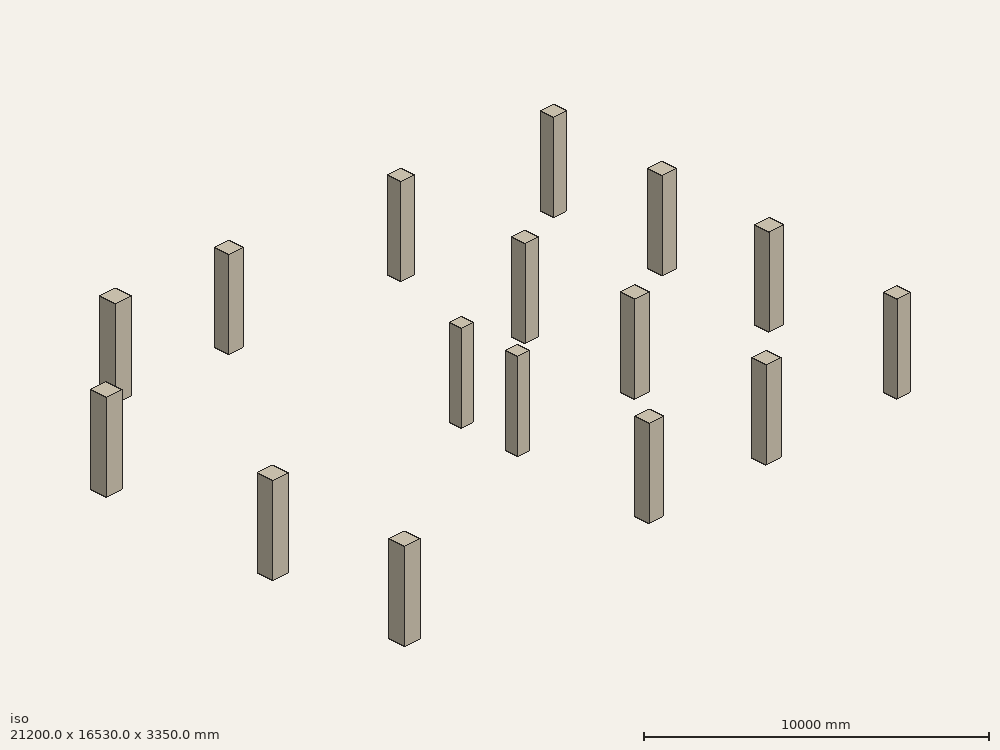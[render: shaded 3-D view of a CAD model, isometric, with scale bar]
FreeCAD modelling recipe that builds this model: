
FCSTD DOCUMENT  (FreeCAD 0.19R24291 (Git))
Label: rashidzadeh
License: All rights reserved
LicenseURL: http://en.wikipedia.org/wiki/All_rights_reserved
objects: Part::Part2DObjectPython×68, Part::FeaturePython×53, App::FeaturePython×17, App::DocumentObjectGroup×5
note: 268 computed .brp shape members not serialized (recipe doc carries the construction recipe); baked Part::Feature solids carry a one-line shape summary decoded from their .brp

FEATURE [Part::Part2DObjectPython] Line006  label="C1_Story1_CenterLine"  # Draft 2D object (typed FeaturePython)
  Area = 0
  ChamferSize = 0
  Closed = false
  End = (17740,20340,3350)
  FilletRadius = 0
  Length = 3350
  MakeFace = true
  Points = (2) [(17740,20340,0),(17740,20340,3350)]
  Start = (17740,20340,0)
  Subdivisions = 0
FEATURE [Part::Part2DObjectPython] C5512C  # Draft 2D object (typed FeaturePython)
  Height = 550
  Width = 550
FEATURE [Part::FeaturePython] Structure  label="C1_Story1"  # Arch/BIM 24 (typed FeaturePython)
  AttacherType = Attacher::AttachEngine3D
  AttachmentOffset = pos=(0,0,0) rot=(0,0,1;1.5708rad)
  Base = -> C5512C
  FaceMaker = 0
  Height = 3350
  HorizontalArea = 302500
  IfcData = attributes={"GlobalId": {"name": "GlobalId", "type": "IfcGloballyUniqueId", "is_enum": false, "enum_values": []}, "Description": {"... (+438 chars omitted),+1 more (map truncated)
  IfcType = 24
  Length = 0
  MapMode = 7
  MoveBase = false
  MoveWithHost = false
  Nodes = (2) [(17740,20340,0),(17740,20340,3350)]
  NodesOffset = 0
  Normal = (0,0,0)
  PerimeterLength = 2200
  Placement = pos=(17740,20340,0) rot=(0,0,1;1.5708rad)
  PredefinedType = 0
  Support = -> [Line006]
  VerticalArea = 7.37e+06
  Width = 200
  combos_load = Combo1 Max=2929.3594, 27006.37, 14808.13,Combo10 Max=2608.538, -98112.68, -391082.9,Combo11 Max=2657.75, -72288.26, -345375.92,+37 more (map truncated)
FEATURE [Part::Part2DObjectPython] Line007  label="C2_Story1_CenterLine"  # Draft 2D object (typed FeaturePython)
  Area = 0
  ChamferSize = 0
  Closed = false
  End = (23500,19838.5,3350)
  FilletRadius = 0
  Length = 3350
  MakeFace = true
  Points = (2) [(23500,19838.5,0),(23500,19838.5,3350)]
  Start = (23500,19838.5,0)
  Subdivisions = 0
FEATURE [Part::FeaturePython] Structure001  label="C2_Story1"  # Arch/BIM 24 (typed FeaturePython)
  AttacherType = Attacher::AttachEngine3D
  AttachmentOffset = pos=(0,0,0) rot=(0,0,1;1.5708rad)
  Base = -> C5512C
  FaceMaker = 0
  Height = 3350
  HorizontalArea = 302500
  IfcData = attributes={"GlobalId": {"name": "GlobalId", "type": "IfcGloballyUniqueId", "is_enum": false, "enum_values": []}, "Description": {"... (+438 chars omitted),+1 more (map truncated)
  IfcType = 24
  Length = 0
  MapMode = 7
  MoveBase = false
  MoveWithHost = false
  Nodes = (2) [(23500,19838.5,0),(23500,19838.5,3350)]
  NodesOffset = 0
  Normal = (0,0,0)
  PerimeterLength = 2200
  Placement = pos=(23500,19838.5,0) rot=(0,0,1;1.5708rad)
  PredefinedType = 0
  Support = -> [Line007]
  VerticalArea = 7.37e+06
  Width = 200
  combos_load = Combo1 Max=1754.8461, 12356.17, -26849.18,Combo10 Max=2143.525, -139905.36, -387343.42,Combo11 Max=2175.8338, -83310.12, -350318.73,+37 more (map truncated)
FEATURE [Part::Part2DObjectPython] Line008  label="C17_Story1_CenterLine"  # Draft 2D object (typed FeaturePython)
  Area = 0
  ChamferSize = 0
  Closed = false
  End = (23370,15250,3350)
  FilletRadius = 0
  Length = 3350
  MakeFace = true
  Points = (2) [(23370,15250,0),(23370,15250,3350)]
  Start = (23370,15250,0)
  Subdivisions = 0
FEATURE [Part::Part2DObjectPython] C6012AC  # Draft 2D object (typed FeaturePython)
  Height = 600
  Width = 600
FEATURE [Part::FeaturePython] Structure002  label="C17_Story1"  # Arch/BIM 24 (typed FeaturePython)
  AttacherType = Attacher::AttachEngine3D
  AttachmentOffset = pos=(0,0,0) rot=(0,0,1;1.5708rad)
  Base = -> C6012AC
  FaceMaker = 0
  Height = 3350
  HorizontalArea = 360000
  IfcData = attributes={"GlobalId": {"name": "GlobalId", "type": "IfcGloballyUniqueId", "is_enum": false, "enum_values": []}, "Description": {"... (+438 chars omitted),+1 more (map truncated)
  IfcType = 24
  Length = 0
  MapMode = 7
  MoveBase = false
  MoveWithHost = false
  Nodes = (2) [(23370,15250,0),(23370,15250,3350)]
  NodesOffset = 0
  Normal = (0,0,0)
  PerimeterLength = 2400
  Placement = pos=(23370,15250,0) rot=(0,0,1;1.5708rad)
  PredefinedType = 0
  Support = -> [Line008]
  VerticalArea = 8.04e+06
  Width = 200
  combos_load = Combo1 Max=1514.2218, -5536.02, -34563.49,Combo10 Max=1873.5598, -222983.25, -488160.13,Combo11 Max=1871.0673, -140666.82, -475481.05,+37 more (map truncated)
FEATURE [Part::Part2DObjectPython] Line009  label="C18_Story1_CenterLine"  # Draft 2D object (typed FeaturePython)
  Area = 0
  ChamferSize = 0
  Closed = false
  End = (23250,10750,3350)
  FilletRadius = 0
  Length = 3350
  MakeFace = true
  Points = (2) [(23250,10750,0),(23250,10750,3350)]
  Start = (23250,10750,0)
  Subdivisions = 0
FEATURE [Part::FeaturePython] Structure003  label="C18_Story1"  # Arch/BIM 24 (typed FeaturePython)
  AttacherType = Attacher::AttachEngine3D
  AttachmentOffset = pos=(0,0,0) rot=(0,0,1;1.5708rad)
  Base = -> C6012AC
  FaceMaker = 0
  Height = 3350
  HorizontalArea = 360000
  IfcData = attributes={"GlobalId": {"name": "GlobalId", "type": "IfcGloballyUniqueId", "is_enum": false, "enum_values": []}, "Description": {"... (+438 chars omitted),+1 more (map truncated)
  IfcType = 24
  Length = 0
  MapMode = 7
  MoveBase = false
  MoveWithHost = false
  Nodes = (2) [(23250,10750,0),(23250,10750,3350)]
  NodesOffset = 0
  Normal = (0,0,0)
  PerimeterLength = 2400
  Placement = pos=(23250,10750,0) rot=(0,0,1;1.5708rad)
  PredefinedType = 0
  Support = -> [Line009]
  VerticalArea = 8.04e+06
  Width = 200
  combos_load = Combo1 Max=1534.3408, 49.31, -39260.22,Combo10 Max=2051.3394, -213536.56, -457180.36,Combo11 Max=2057.4036, -133173.75, -478456.04,+37 more (map truncated)
FEATURE [Part::Part2DObjectPython] Line010  label="C5_Story1_CenterLine"  # Draft 2D object (typed FeaturePython)
  Area = 0
  ChamferSize = 0
  Closed = false
  End = (17740,5350,3350)
  FilletRadius = 0
  Length = 3350
  MakeFace = true
  Points = (2) [(17740,5350,0),(17740,5350,3350)]
  Start = (17740,5350,0)
  Subdivisions = 0
FEATURE [Part::FeaturePython] Structure004  label="C5_Story1"  # Arch/BIM 24 (typed FeaturePython)
  AttacherType = Attacher::AttachEngine3D
  AttachmentOffset = pos=(0,0,0) rot=(0,0,1;1.5708rad)
  Base = -> C6012AC
  FaceMaker = 0
  Height = 3350
  HorizontalArea = 360000
  IfcData = attributes={"GlobalId": {"name": "GlobalId", "type": "IfcGloballyUniqueId", "is_enum": false, "enum_values": []}, "Description": {"... (+438 chars omitted),+1 more (map truncated)
  IfcType = 24
  Length = 0
  MapMode = 7
  MoveBase = false
  MoveWithHost = false
  Nodes = (2) [(17740,5350,0),(17740,5350,3350)]
  NodesOffset = 0
  Normal = (0,0,0)
  PerimeterLength = 2400
  Placement = pos=(17740,5350,0) rot=(0,0,1;1.5708rad)
  PredefinedType = 0
  Support = -> [Line010]
  VerticalArea = 8.04e+06
  Width = 200
  combos_load = Combo1 Max=1623.3033, -947.79, -5177.17,Combo10 Max=1786.5067, -169313.57, -460450.33,Combo11 Max=1770.754, -135335.23, -531760.45,+37 more (map truncated)
FEATURE [Part::Part2DObjectPython] Line011  label="C6_Story1_CenterLine"  # Draft 2D object (typed FeaturePython)
  Area = 0
  ChamferSize = 0
  Closed = false
  End = (12940,5350,3350)
  FilletRadius = 0
  Length = 3350
  MakeFace = true
  Points = (2) [(12940,5350,0),(12940,5350,3350)]
  Start = (12940,5350,0)
  Subdivisions = 0
FEATURE [Part::FeaturePython] Structure005  label="C6_Story1"  # Arch/BIM 24 (typed FeaturePython)
  AttacherType = Attacher::AttachEngine3D
  AttachmentOffset = pos=(0,0,0) rot=(0,0,1;1.5708rad)
  Base = -> C6012AC
  FaceMaker = 0
  Height = 3350
  HorizontalArea = 360000
  IfcData = attributes={"GlobalId": {"name": "GlobalId", "type": "IfcGloballyUniqueId", "is_enum": false, "enum_values": []}, "Description": {"... (+438 chars omitted),+1 more (map truncated)
  IfcType = 24
  Length = 0
  MapMode = 7
  MoveBase = false
  MoveWithHost = false
  Nodes = (2) [(12940,5350,0),(12940,5350,3350)]
  NodesOffset = 0
  Normal = (0,0,0)
  PerimeterLength = 2400
  Placement = pos=(12940,5350,0) rot=(0,0,1;1.5708rad)
  PredefinedType = 0
  Support = -> [Line011]
  VerticalArea = 8.04e+06
  Width = 200
  combos_load = Combo1 Max=2458.9073, 10889.53, -106700.8,Combo10 Max=1939.8727, -132976.26, -554878.34,Combo11 Max=1860.3718, -132910.34, -622641.45,+37 more (map truncated)
FEATURE [Part::Part2DObjectPython] Line012  label="C19_Story1_CenterLine"  # Draft 2D object (typed FeaturePython)
  Area = 0
  ChamferSize = 0
  Closed = false
  End = (23100,5350,3350)
  FilletRadius = 0
  Length = 3350
  MakeFace = true
  Points = (2) [(23100,5350,0),(23100,5350,3350)]
  Start = (23100,5350,0)
  Subdivisions = 0
FEATURE [Part::Part2DObjectPython] C5512AC  # Draft 2D object (typed FeaturePython)
  Height = 550
  Width = 550
FEATURE [Part::FeaturePython] Structure006  label="C19_Story1"  # Arch/BIM 24 (typed FeaturePython)
  AttacherType = Attacher::AttachEngine3D
  AttachmentOffset = pos=(0,0,0) rot=(0,0,1;1.5708rad)
  Base = -> C5512AC
  FaceMaker = 0
  Height = 3350
  HorizontalArea = 302500
  IfcData = attributes={"GlobalId": {"name": "GlobalId", "type": "IfcGloballyUniqueId", "is_enum": false, "enum_values": []}, "Description": {"... (+438 chars omitted),+1 more (map truncated)
  IfcType = 24
  Length = 0
  MapMode = 7
  MoveBase = false
  MoveWithHost = false
  Nodes = (2) [(23100,5350,0),(23100,5350,3350)]
  NodesOffset = 0
  Normal = (0,0,0)
  PerimeterLength = 2200
  Placement = pos=(23100,5350,0) rot=(0,0,1;1.5708rad)
  PredefinedType = 0
  Support = -> [Line012]
  VerticalArea = 7.37e+06
  Width = 200
  combos_load = Combo1 Max=1051.5097, -14568.81, -35137.32,Combo10 Max=1680.8499, -155391.05, -323776.55,Combo11 Max=1698.4736, -101933.47, -370507.25,+37 more (map truncated)
FEATURE [Part::Part2DObjectPython] Line013  label="C8_Story1_CenterLine"  # Draft 2D object (typed FeaturePython)
  Area = 0
  ChamferSize = 0
  Closed = false
  End = (11240,20890,3350)
  FilletRadius = 0
  Length = 3350
  MakeFace = true
  Points = (2) [(11240,20890,0),(11240,20890,3350)]
  Start = (11240,20890,0)
  Subdivisions = 0
FEATURE [Part::Part2DObjectPython] C6012C  # Draft 2D object (typed FeaturePython)
  Height = 600
  Width = 600
FEATURE [Part::FeaturePython] Structure007  label="C8_Story1"  # Arch/BIM 24 (typed FeaturePython)
  AttacherType = Attacher::AttachEngine3D
  AttachmentOffset = pos=(0,0,0) rot=(0,0,1;1.5708rad)
  Base = -> C6012C
  FaceMaker = 0
  Height = 3350
  HorizontalArea = 360000
  IfcData = attributes={"GlobalId": {"name": "GlobalId", "type": "IfcGloballyUniqueId", "is_enum": false, "enum_values": []}, "Description": {"... (+438 chars omitted),+1 more (map truncated)
  IfcType = 24
  Length = 0
  MapMode = 7
  MoveBase = false
  MoveWithHost = false
  Nodes = (2) [(11240,20890,0),(11240,20890,3350)]
  NodesOffset = 0
  Normal = (0,0,0)
  PerimeterLength = 2400
  Placement = pos=(11240,20890,0) rot=(0,0,1;1.5708rad)
  PredefinedType = 0
  Support = -> [Line013]
  VerticalArea = 8.04e+06
  Width = 200
  combos_load = Combo1 Max=3176.7816, 67519.66, -1586.57,Combo10 Max=3690.7518, -72646.95, -573333.56,Combo11 Max=3628.5505, -82554.37, -507645.57,+37 more (map truncated)
FEATURE [Part::Part2DObjectPython] Line014  label="C9_Story1_CenterLine"  # Draft 2D object (typed FeaturePython)
  Area = 0
  ChamferSize = 0
  Closed = false
  End = (6930,21230,3350)
  FilletRadius = 0
  Length = 3350
  MakeFace = true
  Points = (2) [(6930,21230,0),(6930,21230,3350)]
  Start = (6930,21230,0)
  Subdivisions = 0
FEATURE [Part::Part2DObjectPython] C6516AC  # Draft 2D object (typed FeaturePython)
  Height = 650
  Width = 650
FEATURE [Part::FeaturePython] Structure008  label="C9_Story1"  # Arch/BIM 24 (typed FeaturePython)
  AttacherType = Attacher::AttachEngine3D
  AttachmentOffset = pos=(0,0,0) rot=(0,0,1;1.5708rad)
  Base = -> C6516AC
  FaceMaker = 0
  Height = 3350
  HorizontalArea = 422500
  IfcData = attributes={"GlobalId": {"name": "GlobalId", "type": "IfcGloballyUniqueId", "is_enum": false, "enum_values": []}, "Description": {"... (+438 chars omitted),+1 more (map truncated)
  IfcType = 24
  Length = 0
  MapMode = 7
  MoveBase = false
  MoveWithHost = false
  Nodes = (2) [(6930,21230,0),(6930,21230,3350)]
  NodesOffset = 0
  Normal = (0,0,0)
  PerimeterLength = 2600
  Placement = pos=(6930,21230,0) rot=(0,0,1;1.5708rad)
  PredefinedType = 0
  Support = -> [Line014]
  VerticalArea = 8.71e+06
  Width = 200
  combos_load = Combo1 Max=3178.5002, 13656.36, 31223.41,Combo10 Max=2579.0077, -108238.08, -657320.49,Combo11 Max=2529.7417, -170319.15, -568803.46,+37 more (map truncated)
FEATURE [Part::Part2DObjectPython] Line015  label="C10_Story1_CenterLine"  # Draft 2D object (typed FeaturePython)
  Area = 0
  ChamferSize = 0
  Closed = false
  End = (2900,17580,3350)
  FilletRadius = 0
  Length = 3350
  MakeFace = true
  Points = (2) [(2900,17580,0),(2900,17580,3350)]
  Start = (2900,17580,0)
  Subdivisions = 0
FEATURE [Part::FeaturePython] Structure009  label="C10_Story1"  # Arch/BIM 24 (typed FeaturePython)
  AttacherType = Attacher::AttachEngine3D
  AttachmentOffset = pos=(0,0,0) rot=(0,0,1;1.5708rad)
  Base = -> C6516AC
  FaceMaker = 0
  Height = 3350
  HorizontalArea = 422500
  IfcData = attributes={"GlobalId": {"name": "GlobalId", "type": "IfcGloballyUniqueId", "is_enum": false, "enum_values": []}, "Description": {"... (+438 chars omitted),+1 more (map truncated)
  IfcType = 24
  Length = 0
  MapMode = 7
  MoveBase = false
  MoveWithHost = false
  Nodes = (2) [(2900,17580,0),(2900,17580,3350)]
  NodesOffset = 0
  Normal = (0,0,0)
  PerimeterLength = 2600
  Placement = pos=(2900,17580,0) rot=(0,0,1;1.5708rad)
  PredefinedType = 0
  Support = -> [Line015]
  VerticalArea = 8.71e+06
  Width = 200
  combos_load = Combo1 Max=4513.1788, 66434.1, 128004.31,Combo10 Max=3493.9652, -29609.04, -415032.95,Combo11 Max=3559.9915, -136385.01, -369140.23,+37 more (map truncated)
FEATURE [Part::Part2DObjectPython] Line016  label="C16_Story1_CenterLine"  # Draft 2D object (typed FeaturePython)
  Area = 0
  ChamferSize = 0
  Closed = false
  End = (2900,5350,3350)
  FilletRadius = 0
  Length = 3350
  MakeFace = true
  Points = (2) [(2900,5350,0),(2900,5350,3350)]
  Start = (2900,5350,0)
  Subdivisions = 0
FEATURE [Part::Part2DObjectPython] C6516A  # Draft 2D object (typed FeaturePython)
  Height = 650
  Width = 650
FEATURE [Part::FeaturePython] Structure010  label="C16_Story1"  # Arch/BIM 24 (typed FeaturePython)
  AttacherType = Attacher::AttachEngine3D
  AttachmentOffset = pos=(0,0,0) rot=(0,0,1;1.5708rad)
  Base = -> C6516A
  FaceMaker = 0
  Height = 3350
  HorizontalArea = 422500
  IfcData = attributes={"GlobalId": {"name": "GlobalId", "type": "IfcGloballyUniqueId", "is_enum": false, "enum_values": []}, "Description": {"... (+438 chars omitted),+1 more (map truncated)
  IfcType = 24
  Length = 0
  MapMode = 7
  MoveBase = false
  MoveWithHost = false
  Nodes = (2) [(2900,5350,0),(2900,5350,3350)]
  NodesOffset = 0
  Normal = (0,0,0)
  PerimeterLength = 2600
  Placement = pos=(2900,5350,0) rot=(0,0,1;1.5708rad)
  PredefinedType = 0
  Support = -> [Line016]
  VerticalArea = 8.71e+06
  Width = 200
  combos_load = Combo1 Max=2178.0668, -11443.95, 110544.97,Combo10 Max=2207.6537, -146873.33, -349025.65,Combo11 Max=2312.863, -249404.95, -427796.67,+37 more (map truncated)
FEATURE [Part::Part2DObjectPython] Line017  label="C12_Story1_CenterLine"  # Draft 2D object (typed FeaturePython)
  Area = 0
  ChamferSize = 0
  Closed = false
  End = (17740,10750,3350)
  FilletRadius = 0
  Length = 3350
  MakeFace = true
  Points = (2) [(17740,10750,0),(17740,10750,3350)]
  Start = (17740,10750,0)
  Subdivisions = 0
FEATURE [Part::FeaturePython] Structure011  label="C12_Story1"  # Arch/BIM 24 (typed FeaturePython)
  AttacherType = Attacher::AttachEngine3D
  AttachmentOffset = pos=(0,0,0) rot=(0,0,1;1.5708rad)
  Base = -> C6012C
  FaceMaker = 0
  Height = 3350
  HorizontalArea = 360000
  IfcData = attributes={"GlobalId": {"name": "GlobalId", "type": "IfcGloballyUniqueId", "is_enum": false, "enum_values": []}, "Description": {"... (+438 chars omitted),+1 more (map truncated)
  IfcType = 24
  Length = 0
  MapMode = 7
  MoveBase = false
  MoveWithHost = false
  Nodes = (2) [(17740,10750,0),(17740,10750,3350)]
  NodesOffset = 0
  Normal = (0,0,0)
  PerimeterLength = 2400
  Placement = pos=(17740,10750,0) rot=(0,0,1;1.5708rad)
  PredefinedType = 0
  Support = -> [Line017]
  VerticalArea = 8.04e+06
  Width = 200
  combos_load = Combo1 Max=2372.5516, -20700, 4401.45,Combo10 Max=2415.4815, -204900.61, -476224.38,Combo11 Max=2407.8904, -168225.73, -499976.16,+37 more (map truncated)
FEATURE [Part::Part2DObjectPython] Line018  label="C13_Story1_CenterLine"  # Draft 2D object (typed FeaturePython)
  Area = 0
  ChamferSize = 0
  Closed = false
  End = (17740,15250,3350)
  FilletRadius = 0
  Length = 3350
  MakeFace = true
  Points = (2) [(17740,15250,0),(17740,15250,3350)]
  Start = (17740,15250,0)
  Subdivisions = 0
FEATURE [Part::FeaturePython] Structure012  label="C13_Story1"  # Arch/BIM 24 (typed FeaturePython)
  AttacherType = Attacher::AttachEngine3D
  AttachmentOffset = pos=(0,0,0) rot=(0,0,1;1.5708rad)
  Base = -> C5512C
  FaceMaker = 0
  Height = 3350
  HorizontalArea = 302500
  IfcData = attributes={"GlobalId": {"name": "GlobalId", "type": "IfcGloballyUniqueId", "is_enum": false, "enum_values": []}, "Description": {"... (+438 chars omitted),+1 more (map truncated)
  IfcType = 24
  Length = 0
  MapMode = 7
  MoveBase = false
  MoveWithHost = false
  Nodes = (2) [(17740,15250,0),(17740,15250,3350)]
  NodesOffset = 0
  Normal = (0,0,0)
  PerimeterLength = 2200
  Placement = pos=(17740,15250,0) rot=(0,0,1;1.5708rad)
  PredefinedType = 0
  Support = -> [Line018]
  VerticalArea = 7.37e+06
  Width = 200
  combos_load = Combo1 Max=2562.7432, -8357.02, -515.48,Combo10 Max=2113.2435, -155815.97, -358125.31,Combo11 Max=2129.9271, -128933.56, -347442.14,+37 more (map truncated)
FEATURE [Part::Part2DObjectPython] Line019  label="C14_Story1_CenterLine"  # Draft 2D object (typed FeaturePython)
  Area = 0
  ChamferSize = 0
  Closed = false
  End = (12940,10750,3350)
  FilletRadius = 0
  Length = 3350
  MakeFace = true
  Points = (2) [(12940,10750,0),(12940,10750,3350)]
  Start = (12940,10750,0)
  Subdivisions = 0
FEATURE [Part::Part2DObjectPython] C5012AC  # Draft 2D object (typed FeaturePython)
  Height = 500
  Width = 500
FEATURE [Part::FeaturePython] Structure013  label="C14_Story1"  # Arch/BIM 24 (typed FeaturePython)
  AttacherType = Attacher::AttachEngine3D
  AttachmentOffset = pos=(0,0,0) rot=(0,0,1;3.14159rad)
  Base = -> C5012AC
  FaceMaker = 0
  Height = 3350
  HorizontalArea = 250000
  IfcData = attributes={"GlobalId": {"name": "GlobalId", "type": "IfcGloballyUniqueId", "is_enum": false, "enum_values": []}, "Description": {"... (+438 chars omitted),+1 more (map truncated)
  IfcType = 24
  Length = 0
  MapMode = 7
  MoveBase = false
  MoveWithHost = false
  Nodes = (2) [(12940,10750,0),(12940,10750,3350)]
  NodesOffset = 0
  Normal = (0,0,0)
  PerimeterLength = 2000
  Placement = pos=(12940,10750,0) rot=(0,0,1;3.14159rad)
  PredefinedType = 0
  Support = -> [Line019]
  VerticalArea = 6.7e+06
  Width = 200
  combos_load = Combo1 Max=2582.1087, 172.69, -72462.15,Combo10 Max=2432.6339, -96294.19, -372624.2,Combo11 Max=2403.0715, -96603.51, -385451.48,+37 more (map truncated)
FEATURE [Part::Part2DObjectPython] Line020  label="C15_Story1_CenterLine"  # Draft 2D object (typed FeaturePython)
  Area = 0
  ChamferSize = 0
  Closed = false
  End = (12940,13050,3350)
  FilletRadius = 0
  Length = 3350
  MakeFace = true
  Points = (2) [(12940,13050,0),(12940,13050,3350)]
  Start = (12940,13050,0)
  Subdivisions = 0
FEATURE [Part::Part2DObjectPython] C5016A  # Draft 2D object (typed FeaturePython)
  Height = 500
  Width = 500
FEATURE [Part::FeaturePython] Structure014  label="C15_Story1"  # Arch/BIM 24 (typed FeaturePython)
  AttacherType = Attacher::AttachEngine3D
  AttachmentOffset = pos=(0,0,0) rot=(0,0,1;3.14159rad)
  Base = -> C5016A
  FaceMaker = 0
  Height = 3350
  HorizontalArea = 250000
  IfcData = attributes={"GlobalId": {"name": "GlobalId", "type": "IfcGloballyUniqueId", "is_enum": false, "enum_values": []}, "Description": {"... (+438 chars omitted),+1 more (map truncated)
  IfcType = 24
  Length = 0
  MapMode = 7
  MoveBase = false
  MoveWithHost = false
  Nodes = (2) [(12940,13050,0),(12940,13050,3350)]
  NodesOffset = 0
  Normal = (0,0,0)
  PerimeterLength = 2000
  Placement = pos=(12940,13050,0) rot=(0,0,1;3.14159rad)
  PredefinedType = 0
  Support = -> [Line020]
  VerticalArea = 6.7e+06
  Width = 200
  combos_load = Combo1 Max=3210.485, -73329.89, -94104.41,Combo10 Max=2840.0423, -210175.6, -361309.23,Combo11 Max=2844.4131, -210015.24, -363099.71,+37 more (map truncated)
FEATURE [Part::Part2DObjectPython] Line021  # Draft 2D object (typed FeaturePython)
  Area = 0
  ChamferSize = 0
  Closed = false
  End = (11240,20890,0)
  FilletRadius = 0
  Length = 4323.39
  MakeFace = true
  Points = (2) [(6930,21230,0),(11240,20890,0)]
  Start = (6930,21230,0)
  Subdivisions = 0
  type = Beam
FEATURE [Part::Part2DObjectPython] Line022  # Draft 2D object (typed FeaturePython)
  Area = 0
  ChamferSize = 0
  Closed = false
  End = (17740,20340,0)
  FilletRadius = 0
  Length = 6523.23
  MakeFace = true
  Points = (2) [(11240,20890,0),(17740,20340,0)]
  Start = (11240,20890,0)
  Subdivisions = 0
  type = Beam
FEATURE [Part::Part2DObjectPython] Line023  # Draft 2D object (typed FeaturePython)
  Area = 0
  ChamferSize = 0
  Closed = false
  End = (23500,19838.5,0)
  FilletRadius = 0
  Length = 5781.79
  MakeFace = true
  Points = (2) [(17740,20340,0),(23500,19838.5,0)]
  Start = (17740,20340,0)
  Subdivisions = 0
  type = Beam
FEATURE [Part::Part2DObjectPython] Line024  # Draft 2D object (typed FeaturePython)
  Area = 0
  ChamferSize = 0
  Closed = false
  End = (23500,19838.5,0)
  FilletRadius = 0
  Length = 4590.3
  MakeFace = true
  Points = (2) [(23370,15250,0),(23500,19838.5,0)]
  Start = (23370,15250,0)
  Subdivisions = 0
  type = Beam
FEATURE [Part::Part2DObjectPython] Line025  # Draft 2D object (typed FeaturePython)
  Area = 0
  ChamferSize = 0
  Closed = false
  End = (23370,15250,0)
  FilletRadius = 0
  Length = 4501.6
  MakeFace = true
  Points = (2) [(23250,10750,0),(23370,15250,0)]
  Start = (23250,10750,0)
  Subdivisions = 0
  type = Beam
FEATURE [Part::Part2DObjectPython] Line026  # Draft 2D object (typed FeaturePython)
  Area = 0
  ChamferSize = 0
  Closed = false
  End = (23100,5350,0)
  FilletRadius = 0
  Length = 5360
  MakeFace = true
  Points = (2) [(17740,5350,0),(23100,5350,0)]
  Start = (17740,5350,0)
  Subdivisions = 0
  type = Beam
FEATURE [Part::Part2DObjectPython] Line027  # Draft 2D object (typed FeaturePython)
  Area = 0
  ChamferSize = 0
  Closed = false
  End = (17740,5350,0)
  FilletRadius = 0
  Length = 4800
  MakeFace = true
  Points = (2) [(12940,5350,0),(17740,5350,0)]
  Start = (12940,5350,0)
  Subdivisions = 0
  type = Beam
FEATURE [Part::Part2DObjectPython] Line028  # Draft 2D object (typed FeaturePython)
  Area = 0
  ChamferSize = 0
  Closed = false
  End = (12940,5350,0)
  FilletRadius = 0
  Length = 10040
  MakeFace = true
  Points = (2) [(2900,5350,0),(12940,5350,0)]
  Start = (2900,5350,0)
  Subdivisions = 0
  type = Beam
FEATURE [Part::Part2DObjectPython] Line029  # Draft 2D object (typed FeaturePython)
  Area = 0
  ChamferSize = 0
  Closed = false
  End = (2900,10750,0)
  FilletRadius = 0
  Length = 5400
  MakeFace = true
  Points = (2) [(2900,5350,0),(2900,10750,0)]
  Start = (2900,5350,0)
  Subdivisions = 0
  type = Beam
FEATURE [Part::Part2DObjectPython] Line030  # Draft 2D object (typed FeaturePython)
  Area = 0
  ChamferSize = 0
  Closed = false
  End = (2900,17580,0)
  FilletRadius = 0
  Length = 6830
  MakeFace = true
  Points = (2) [(2900,10750,0),(2900,17580,0)]
  Start = (2900,10750,0)
  Subdivisions = 0
  type = Beam
FEATURE [Part::Part2DObjectPython] Line031  # Draft 2D object (typed FeaturePython)
  Area = 0
  ChamferSize = 0
  Closed = false
  End = (6930,21230,0)
  FilletRadius = 0
  Length = 5437.22
  MakeFace = true
  Points = (2) [(2900,17580,0),(6930,21230,0)]
  Start = (2900,17580,0)
  Subdivisions = 0
  type = Beam
FEATURE [Part::Part2DObjectPython] Line032  # Draft 2D object (typed FeaturePython)
  Area = 0
  ChamferSize = 0
  Closed = false
  End = (17740,10750,0)
  FilletRadius = 0
  Length = 5400
  MakeFace = true
  Points = (2) [(17740,5350,0),(17740,10750,0)]
  Start = (17740,5350,0)
  Subdivisions = 0
  type = Beam
FEATURE [Part::Part2DObjectPython] Line033  # Draft 2D object (typed FeaturePython)
  Area = 0
  ChamferSize = 0
  Closed = false
  End = (17740,15250,0)
  FilletRadius = 0
  Length = 4500
  MakeFace = true
  Points = (2) [(17740,10750,0),(17740,15250,0)]
  Start = (17740,10750,0)
  Subdivisions = 0
  type = Beam
FEATURE [Part::Part2DObjectPython] Line034  # Draft 2D object (typed FeaturePython)
  Area = 0
  ChamferSize = 0
  Closed = false
  End = (12940,10750,0)
  FilletRadius = 0
  Length = 5400
  MakeFace = true
  Points = (2) [(12940,5350,0),(12940,10750,0)]
  Start = (12940,5350,0)
  Subdivisions = 0
  type = Beam
FEATURE [Part::Part2DObjectPython] Line035  # Draft 2D object (typed FeaturePython)
  Area = 0
  ChamferSize = 0
  Closed = false
  End = (12940,13050,0)
  FilletRadius = 0
  Length = 2300
  MakeFace = true
  Points = (2) [(12940,10750,0),(12940,13050,0)]
  Start = (12940,10750,0)
  Subdivisions = 0
  type = Beam
FEATURE [Part::Part2DObjectPython] Line036  # Draft 2D object (typed FeaturePython)
  Area = 0
  ChamferSize = 0
  Closed = false
  End = (12940,13050,0)
  FilletRadius = 0
  Length = 8022.19
  MakeFace = true
  Points = (2) [(11240,20890,0),(12940,13050,0)]
  Start = (11240,20890,0)
  Subdivisions = 0
  type = Beam
FEATURE [Part::Part2DObjectPython] Line037  # Draft 2D object (typed FeaturePython)
  Area = 0
  ChamferSize = 0
  Closed = false
  End = (23250,10750,0)
  FilletRadius = 0
  Length = 5510
  MakeFace = true
  Points = (2) [(17740,10750,0),(23250,10750,0)]
  Start = (17740,10750,0)
  Subdivisions = 0
  type = Beam
FEATURE [Part::Part2DObjectPython] Line038  # Draft 2D object (typed FeaturePython)
  Area = 0
  ChamferSize = 0
  Closed = false
  End = (17740,10750,0)
  FilletRadius = 0
  Length = 4800
  MakeFace = true
  Points = (2) [(12940,10750,0),(17740,10750,0)]
  Start = (12940,10750,0)
  Subdivisions = 0
  type = Beam
FEATURE [Part::Part2DObjectPython] Line039  # Draft 2D object (typed FeaturePython)
  Area = 0
  ChamferSize = 0
  Closed = false
  End = (12940,10750,0)
  FilletRadius = 0
  Length = 10040
  MakeFace = true
  Points = (2) [(2900,10750,0),(12940,10750,0)]
  Start = (2900,10750,0)
  Subdivisions = 0
  type = Beam
FEATURE [Part::Part2DObjectPython] Line040  # Draft 2D object (typed FeaturePython)
  Area = 0
  ChamferSize = 0
  Closed = false
  End = (12940,13050,0)
  FilletRadius = 0
  Length = 11014.6
  MakeFace = true
  Points = (2) [(2900,17580,0),(12940,13050,0)]
  Start = (2900,17580,0)
  Subdivisions = 0
  type = Beam
FEATURE [Part::Part2DObjectPython] Line041  # Draft 2D object (typed FeaturePython)
  Area = 0
  ChamferSize = 0
  Closed = false
  End = (23370,15250,0)
  FilletRadius = 0
  Length = 5630
  MakeFace = true
  Points = (2) [(17740,15250,0),(23370,15250,0)]
  Start = (17740,15250,0)
  Subdivisions = 0
  type = Beam
FEATURE [Part::Part2DObjectPython] Line042  label="C11_Story1_CenterLine"  # Draft 2D object (typed FeaturePython)
  Area = 0
  ChamferSize = 0
  Closed = false
  End = (2900,10750,3350)
  FilletRadius = 0
  Length = 3350
  MakeFace = true
  Points = (2) [(2900,10750,0),(2900,10750,3350)]
  Start = (2900,10750,0)
  Subdivisions = 0
FEATURE [Part::FeaturePython] Structure015  label="C11_Story1"  # Arch/BIM 24 (typed FeaturePython)
  AttacherType = Attacher::AttachEngine3D
  AttachmentOffset = pos=(0,0,0) rot=(0,0,1;1.5708rad)
  Base = -> C6516A
  FaceMaker = 0
  Height = 3350
  HorizontalArea = 422500
  IfcData = attributes={"GlobalId": {"name": "GlobalId", "type": "IfcGloballyUniqueId", "is_enum": false, "enum_values": []}, "Description": {"... (+438 chars omitted),+1 more (map truncated)
  IfcType = 24
  Length = 0
  MapMode = 7
  MoveBase = false
  MoveWithHost = false
  Nodes = (2) [(2900,10750,0),(2900,10750,3350)]
  NodesOffset = 0
  Normal = (0,0,0)
  PerimeterLength = 2600
  Placement = pos=(2900,10750,0) rot=(0,0,1;1.5708rad)
  PredefinedType = 0
  Support = -> [Line042]
  VerticalArea = 8.71e+06
  Width = 200
  combos_load = Combo1 Max=3352.5419, -47728.92, 119986.56,Combo10 Max=3085.1187, -203250.05, -354468.47,Combo11 Max=3033.9869, -319766.11, -381702.35,+37 more (map truncated)
FEATURE [App::DocumentObjectGroup] Columns
  Group = -> [Structure,Structure001,Structure002,Structure003,Structure004,Structure005,Structure006,Structure007,Structure008,Structure009,Structure010,Structure011,Structure012,Structure013,Structure014,Structure015]
FEATURE [Part::Part2DObjectPython] Line043  # Draft 2D object (typed FeaturePython)
  Area = 0
  ChamferSize = 0
  Closed = false
  End = (17740,13050,0)
  FilletRadius = 0
  Length = 4800
  MakeFace = true
  Points = (2) [(12940,13050,0),(17740,13050,0)]
  Start = (12940,13050,0)
  Subdivisions = 0
  type = Beam
FEATURE [Part::Part2DObjectPython] Line047  # Draft 2D object (typed FeaturePython)
  Area = 0
  ChamferSize = 0
  Closed = false
  End = (17740,20340,0)
  FilletRadius = 0
  Length = 5090
  MakeFace = true
  Points = (2) [(17740,15250,0),(17740,20340,0)]
  Start = (17740,15250,0)
  Subdivisions = 0
  type = Beam
FEATURE [Part::Part2DObjectPython] Line048  # Draft 2D object (typed FeaturePython)
  Area = 0
  ChamferSize = 0
  Closed = false
  End = (23250,10750,0)
  FilletRadius = 0
  Length = 5402.08
  MakeFace = true
  Points = (2) [(23100,5350,0),(23250,10750,0)]
  Start = (23100,5350,0)
  Subdivisions = 0
  type = Beam
FEATURE [App::DocumentObjectGroup] Beams
  Group = -> [Line021,Line022,Line023,Line024,Line025,Line026,Line027,Line028,Line029,Line030,Line031,Line032,Line033,Line034,Line035,Line036,Line037,Line038,Line039,Line040,Line041,Line043,Line047,Line048]
FEATURE [App::FeaturePython] Safe  # WARN: FeaturePython — macro-defined, semantics opaque (R4)
  input = <path>
  output = <path>
FEATURE [Part::Part2DObjectPython] Wire  # Draft 2D object (typed FeaturePython)
  Area = 0
  ChamferSize = 0
  Closed = false
  End = (2900,17580,0)
  FilletRadius = 0
  Length = 12230
  MakeFace = false
  Points = (3) [(2900,5350,0),(2900,10750,0),(2900,17580,0)]
  Start = (2900,5350,0)
  Subdivisions = 0
FEATURE [Part::FeaturePython] BaseFoundation  # Arch/BIM 77 (typed FeaturePython)
  Base = -> Wire
  HorizontalArea = 0
  IfcData = attributes={"GlobalId": {"name": "GlobalId", "type": "IfcGloballyUniqueId", "is_enum": false, "enum_values": []}, "Description": {"... (+511 chars omitted),+1 more (map truncated)
  IfcType = 77
  MoveBase = false
  MoveWithHost = false
  PerimeterLength = 0
  PredefinedType = 0
  VerticalArea = 0
  align = 0
  design_type = 0
  fc = 25000
  final_wire_first_point = (0,0,0)
  final_wire_last_point = (0,0,0)
  height = 1000
  ks = 2
  layer = 1
  left_width = 500
  right_width = 500
  width = 1000
FEATURE [Part::Part2DObjectPython] Wire001  # Draft 2D object (typed FeaturePython)
  Area = 0
  ChamferSize = 0
  Closed = false
  End = (23100,5350,0)
  FilletRadius = 0
  Length = 20200
  MakeFace = false
  Points = (4) [(2900,5350,0),(12940,5350,0),(17740,5350,0),(23100,5350,0)]
  Start = (2900,5350,0)
  Subdivisions = 0
FEATURE [Part::FeaturePython] BaseFoundation001  # Arch/BIM 77 (typed FeaturePython)
  Base = -> Wire001
  HorizontalArea = 0
  IfcData = attributes={"GlobalId": {"name": "GlobalId", "type": "IfcGloballyUniqueId", "is_enum": false, "enum_values": []}, "Description": {"... (+511 chars omitted),+1 more (map truncated)
  IfcType = 77
  MoveBase = false
  MoveWithHost = false
  PerimeterLength = 0
  PredefinedType = 0
  VerticalArea = 0
  align = 0
  design_type = 0
  fc = 25000
  final_wire_first_point = (0,0,0)
  final_wire_last_point = (0,0,0)
  height = 1000
  ks = 2
  layer = 0
  left_width = 500
  right_width = 500
  width = 1000
FEATURE [Part::Part2DObjectPython] Wire002  # Draft 2D object (typed FeaturePython)
  Area = 0
  ChamferSize = 0
  Closed = false
  End = (23250,10750,0)
  FilletRadius = 0
  Length = 20350
  MakeFace = false
  Points = (4) [(2900,10750,0),(12940,10750,0),(17740,10750,0),(23250,10750,0)]
  Start = (2900,10750,0)
  Subdivisions = 0
FEATURE [Part::FeaturePython] BaseFoundation002  # Arch/BIM 77 (typed FeaturePython)
  Base = -> Wire002
  HorizontalArea = 0
  IfcData = attributes={"GlobalId": {"name": "GlobalId", "type": "IfcGloballyUniqueId", "is_enum": false, "enum_values": []}, "Description": {"... (+511 chars omitted),+1 more (map truncated)
  IfcType = 77
  MoveBase = false
  MoveWithHost = false
  PerimeterLength = 0
  PredefinedType = 0
  VerticalArea = 0
  align = 0
  design_type = 0
  fc = 25000
  final_wire_first_point = (0,0,0)
  final_wire_last_point = (0,0,0)
  height = 1000
  ks = 2
  layer = 0
  left_width = 500
  right_width = 500
  width = 1000
FEATURE [Part::Part2DObjectPython] Line  # Draft 2D object (typed FeaturePython)
  Area = 0
  ChamferSize = 0
  Closed = false
  End = (6930,21230,0)
  FilletRadius = 0
  Length = 5437.22
  MakeFace = false
  Points = (2) [(2900,17580,0),(6930,21230,0)]
  Start = (2900,17580,0)
  Subdivisions = 0
FEATURE [Part::FeaturePython] BaseFoundation003  # Arch/BIM 77 (typed FeaturePython)
  Base = -> Line
  HorizontalArea = 0
  IfcData = attributes={"GlobalId": {"name": "GlobalId", "type": "IfcGloballyUniqueId", "is_enum": false, "enum_values": []}, "Description": {"... (+511 chars omitted),+1 more (map truncated)
  IfcType = 77
  MoveBase = false
  MoveWithHost = false
  PerimeterLength = 0
  PredefinedType = 0
  VerticalArea = 0
  align = 0
  design_type = 0
  fc = 25000
  final_wire_first_point = (0,0,0)
  final_wire_last_point = (0,0,0)
  height = 1000
  ks = 2
  layer = 0
  left_width = 500
  right_width = 500
  width = 1000
FEATURE [Part::Part2DObjectPython] Wire003  # Draft 2D object (typed FeaturePython)
  Area = 0
  ChamferSize = 0
  Closed = false
  End = (17740,13050,0)
  FilletRadius = 0
  Length = 15814.6
  MakeFace = false
  Points = (3) [(2900,17580,0),(12940,13050,0),(17740,13050,0)]
  Start = (2900,17580,0)
  Subdivisions = 0
FEATURE [Part::FeaturePython] BaseFoundation004  # Arch/BIM 77 (typed FeaturePython)
  Base = -> Wire003
  HorizontalArea = 0
  IfcData = attributes={"GlobalId": {"name": "GlobalId", "type": "IfcGloballyUniqueId", "is_enum": false, "enum_values": []}, "Description": {"... (+511 chars omitted),+1 more (map truncated)
  IfcType = 77
  MoveBase = false
  MoveWithHost = false
  PerimeterLength = 0
  PredefinedType = 0
  VerticalArea = 0
  align = 0
  design_type = 0
  fc = 25000
  final_wire_first_point = (0,0,0)
  final_wire_last_point = (0,0,0)
  height = 1000
  ks = 2
  layer = 0
  left_width = 500
  right_width = 500
  width = 1000
FEATURE [Part::Part2DObjectPython] Wire004  # Draft 2D object (typed FeaturePython)
  Area = 0
  ChamferSize = 0
  Closed = false
  End = (23500,19838.5,0)
  FilletRadius = 0
  Length = 16628.4
  MakeFace = false
  Points = (4) [(6930,21230,0),(11240,20890,0),(17740,20340,0),(23500,19838.5,0)]
  Start = (6930,21230,0)
  Subdivisions = 0
FEATURE [Part::FeaturePython] BaseFoundation005  # Arch/BIM 77 (typed FeaturePython)
  Base = -> Wire004
  HorizontalArea = 0
  IfcData = attributes={"GlobalId": {"name": "GlobalId", "type": "IfcGloballyUniqueId", "is_enum": false, "enum_values": []}, "Description": {"... (+511 chars omitted),+1 more (map truncated)
  IfcType = 77
  MoveBase = false
  MoveWithHost = false
  PerimeterLength = 0
  PredefinedType = 0
  VerticalArea = 0
  align = 0
  design_type = 0
  fc = 25000
  final_wire_first_point = (0,0,0)
  final_wire_last_point = (0,0,0)
  height = 1000
  ks = 2
  layer = 0
  left_width = 500
  right_width = 500
  width = 1000
FEATURE [Part::Part2DObjectPython] Wire005  # Draft 2D object (typed FeaturePython)
  Area = 0
  ChamferSize = 0
  Closed = false
  End = (12940,5350,0)
  FilletRadius = 0
  Length = 15722.2
  MakeFace = false
  Points = (4) [(11240,20890,0),(12940,13050,0),(12940,10750,0),(12940,5350,0)]
  Start = (11240,20890,0)
  Subdivisions = 0
FEATURE [Part::FeaturePython] BaseFoundation006  # Arch/BIM 77 (typed FeaturePython)
  Base = -> Wire005
  HorizontalArea = 0
  IfcData = attributes={"GlobalId": {"name": "GlobalId", "type": "IfcGloballyUniqueId", "is_enum": false, "enum_values": []}, "Description": {"... (+511 chars omitted),+1 more (map truncated)
  IfcType = 77
  MoveBase = false
  MoveWithHost = false
  PerimeterLength = 0
  PredefinedType = 0
  VerticalArea = 0
  align = 0
  design_type = 0
  fc = 25000
  final_wire_first_point = (0,0,0)
  final_wire_last_point = (0,0,0)
  height = 1000
  ks = 2
  layer = 1
  left_width = 500
  right_width = 500
  width = 1000
FEATURE [Part::Part2DObjectPython] Wire006  # Draft 2D object (typed FeaturePython)
  Area = 0
  ChamferSize = 0
  Closed = false
  End = (17740,20340,0)
  FilletRadius = 0
  Length = 14990
  MakeFace = false
  Points = (4) [(17740,5350,0),(17740,10750,0),(17740,15250,0),(17740,20340,0)]
  Start = (17740,5350,0)
  Subdivisions = 0
FEATURE [Part::FeaturePython] BaseFoundation007  # Arch/BIM 77 (typed FeaturePython)
  Base = -> Wire006
  HorizontalArea = 0
  IfcData = attributes={"GlobalId": {"name": "GlobalId", "type": "IfcGloballyUniqueId", "is_enum": false, "enum_values": []}, "Description": {"... (+511 chars omitted),+1 more (map truncated)
  IfcType = 77
  MoveBase = false
  MoveWithHost = false
  PerimeterLength = 0
  PredefinedType = 0
  VerticalArea = 0
  align = 0
  design_type = 0
  fc = 25000
  final_wire_first_point = (0,0,0)
  final_wire_last_point = (0,0,0)
  height = 1000
  ks = 2
  layer = 1
  left_width = 500
  right_width = 500
  width = 1000
FEATURE [Part::Part2DObjectPython] Line049  # Draft 2D object (typed FeaturePython)
  Area = 0
  ChamferSize = 0
  Closed = false
  End = (23370,15250,0)
  FilletRadius = 0
  Length = 5630
  MakeFace = false
  Points = (2) [(17740,15250,0),(23370,15250,0)]
  Start = (17740,15250,0)
  Subdivisions = 0
FEATURE [Part::FeaturePython] BaseFoundation008  # Arch/BIM 77 (typed FeaturePython)
  Base = -> Line049
  HorizontalArea = 0
  IfcData = attributes={"GlobalId": {"name": "GlobalId", "type": "IfcGloballyUniqueId", "is_enum": false, "enum_values": []}, "Description": {"... (+511 chars omitted),+1 more (map truncated)
  IfcType = 77
  MoveBase = false
  MoveWithHost = false
  PerimeterLength = 0
  PredefinedType = 0
  VerticalArea = 0
  align = 0
  design_type = 0
  fc = 25000
  final_wire_first_point = (0,0,0)
  final_wire_last_point = (0,0,0)
  height = 1000
  ks = 2
  layer = 0
  left_width = 500
  right_width = 500
  width = 1000
FEATURE [Part::Part2DObjectPython] Wire007  # Draft 2D object (typed FeaturePython)
  Area = 0
  ChamferSize = 0
  Closed = false
  End = (23500,19838.5,0)
  FilletRadius = 0
  Length = 14494
  MakeFace = false
  Points = (4) [(23100,5350,0),(23250,10750,0),(23370,15250,0),(23500,19838.5,0)]
  Start = (23100,5350,0)
  Subdivisions = 0
FEATURE [Part::FeaturePython] BaseFoundation009  # Arch/BIM 77 (typed FeaturePython)
  Base = -> Wire007
  HorizontalArea = 0
  IfcData = attributes={"GlobalId": {"name": "GlobalId", "type": "IfcGloballyUniqueId", "is_enum": false, "enum_values": []}, "Description": {"... (+511 chars omitted),+1 more (map truncated)
  IfcType = 77
  MoveBase = false
  MoveWithHost = false
  PerimeterLength = 0
  PredefinedType = 0
  VerticalArea = 0
  align = 0
  design_type = 0
  fc = 25000
  final_wire_first_point = (0,0,0)
  final_wire_last_point = (0,0,0)
  height = 1000
  ks = 2
  layer = 1
  left_width = 500
  right_width = 500
  width = 1000
FEATURE [Part::FeaturePython] Foundation  # Arch/BIM 77 (typed FeaturePython)
  HorizontalArea = 0
  IfcType = 77
  MoveBase = false
  MoveWithHost = false
  PerimeterLength = 0
  VerticalArea = 0
  base_foundations = -> [BaseFoundation,BaseFoundation001,BaseFoundation002,BaseFoundation003,BaseFoundation004,BaseFoundation005,BaseFoundation006,BaseFoundation007,BaseFoundation008,BaseFoundation009]
  continuous_layer = 0
  cover = 75
  d = 775
  fc = 25000
  foundation_type = 0
  height = 850
  height_punch = 850
  ks = 2
  level = 0
  redraw = false
  split = true
  volume = 115.321
FEATURE [Part::Part2DObjectPython] Line050  # Draft 2D object (typed FeaturePython)
  Area = 0
  ChamferSize = 0
  Closed = false
  End = (2900,18128.5,0)
  FilletRadius = 0
  Length = 13278.5
  MakeFace = false
  Points = (2) [(2900,4850,0),(2900,18128.5,0)]
  Start = (2900,4850,0)
  Subdivisions = 0
FEATURE [Part::FeaturePython] Strip  label="CSB1"  # Arch/BIM 0 (typed FeaturePython)
  Base = -> Line050
  HorizontalArea = 0
  IfcData = attributes={"GlobalId": {"name": "GlobalId", "type": "IfcGloballyUniqueId", "is_enum": false, "enum_values": []}, "Description": {"... (+538 chars omitted),+1 more (map truncated)
  IfcType = 0
  MoveBase = false
  MoveWithHost = false
  PerimeterLength = 0
  PredefinedType = 0
  VerticalArea = 0
  align = 0
  design_type = 0
  layer = 1
  left_width = 500
  right_width = 500
  width = 1000
FEATURE [Part::Part2DObjectPython] Line051  # Draft 2D object (typed FeaturePython)
  Area = 0
  ChamferSize = 0
  Closed = false
  End = (23600.2,5350,0)
  FilletRadius = 0
  Length = 21200.2
  MakeFace = false
  Points = (2) [(2400,5350,0),(23600.2,5350,0)]
  Start = (2400,5350,0)
  Subdivisions = 0
FEATURE [Part::FeaturePython] Strip001  label="CSA1"  # Arch/BIM 0 (typed FeaturePython)
  Base = -> Line051
  HorizontalArea = 0
  IfcData = attributes={"GlobalId": {"name": "GlobalId", "type": "IfcGloballyUniqueId", "is_enum": false, "enum_values": []}, "Description": {"... (+538 chars omitted),+1 more (map truncated)
  IfcType = 0
  MoveBase = false
  MoveWithHost = false
  PerimeterLength = 0
  PredefinedType = 0
  VerticalArea = 0
  align = 0
  design_type = 0
  layer = 0
  left_width = 500
  right_width = 500
  width = 1000
FEATURE [Part::Part2DObjectPython] Line052  # Draft 2D object (typed FeaturePython)
  Area = 0
  ChamferSize = 0
  Closed = false
  End = (23750.2,10750,0)
  FilletRadius = 0
  Length = 21350.2
  MakeFace = false
  Points = (2) [(2400,10750,0),(23750.2,10750,0)]
  Start = (2400,10750,0)
  Subdivisions = 0
FEATURE [Part::FeaturePython] Strip002  label="CSA2"  # Arch/BIM 0 (typed FeaturePython)
  Base = -> Line052
  HorizontalArea = 0
  IfcData = attributes={"GlobalId": {"name": "GlobalId", "type": "IfcGloballyUniqueId", "is_enum": false, "enum_values": []}, "Description": {"... (+538 chars omitted),+1 more (map truncated)
  IfcType = 0
  MoveBase = false
  MoveWithHost = false
  PerimeterLength = 0
  PredefinedType = 0
  VerticalArea = 0
  align = 0
  design_type = 0
  layer = 0
  left_width = 500
  right_width = 500
  width = 1000
FEATURE [Part::Part2DObjectPython] Line053  # Draft 2D object (typed FeaturePython)
  Area = 0
  ChamferSize = 0
  Closed = false
  End = (7439.4,21691.4,0)
  FilletRadius = 0
  Length = 6669.92
  MakeFace = false
  Points = (2) [(2495.74,17213.9,0),(7439.4,21691.4,0)]
  Start = (2495.74,17213.9,0)
  Subdivisions = 0
FEATURE [Part::FeaturePython] Strip003  label="CSA3"  # Arch/BIM 0 (typed FeaturePython)
  Base = -> Line053
  HorizontalArea = 0
  IfcData = attributes={"GlobalId": {"name": "GlobalId", "type": "IfcGloballyUniqueId", "is_enum": false, "enum_values": []}, "Description": {"... (+538 chars omitted),+1 more (map truncated)
  IfcType = 0
  MoveBase = false
  MoveWithHost = false
  PerimeterLength = 0
  PredefinedType = 0
  VerticalArea = 0
  align = 0
  design_type = 0
  layer = 0
  left_width = 500
  right_width = 500
  width = 1000
FEATURE [Part::Part2DObjectPython] Wire008  # Draft 2D object (typed FeaturePython)
  Area = 0
  ChamferSize = 0
  Closed = false
  End = (18240,13050,0)
  FilletRadius = 0
  Length = 16860.1
  MakeFace = false
  Points = (3) [(2402.84,17804.3,0),(12940,13050,0),(18240,13050,0)]
  Start = (2402.84,17804.3,0)
  Subdivisions = 0
FEATURE [Part::FeaturePython] Strip004  label="CSA4"  # Arch/BIM 0 (typed FeaturePython)
  Base = -> Wire008
  HorizontalArea = 0
  IfcData = attributes={"GlobalId": {"name": "GlobalId", "type": "IfcGloballyUniqueId", "is_enum": false, "enum_values": []}, "Description": {"... (+538 chars omitted),+1 more (map truncated)
  IfcType = 0
  MoveBase = false
  MoveWithHost = false
  PerimeterLength = 0
  PredefinedType = 0
  VerticalArea = 0
  align = 0
  design_type = 0
  layer = 0
  left_width = 500
  right_width = 500
  width = 1000
FEATURE [Part::Part2DObjectPython] Line054  # Draft 2D object (typed FeaturePython)
  Area = 0
  ChamferSize = 0
  Closed = false
  End = (23999,19795,0)
  FilletRadius = 0
  Length = 17816.5
  MakeFace = false
  Points = (2) [(6244.85,21284,0),(23999,19795,0)]
  Start = (6244.85,21284,0)
  Subdivisions = 0
FEATURE [Part::FeaturePython] Strip005  label="CSA5"  # Arch/BIM 0 (typed FeaturePython)
  Base = -> Line054
  HorizontalArea = 0
  IfcData = attributes={"GlobalId": {"name": "GlobalId", "type": "IfcGloballyUniqueId", "is_enum": false, "enum_values": []}, "Description": {"... (+538 chars omitted),+1 more (map truncated)
  IfcType = 0
  MoveBase = false
  MoveWithHost = false
  PerimeterLength = 0
  PredefinedType = 0
  VerticalArea = 0
  align = 0
  design_type = 0
  layer = 0
  left_width = 500
  right_width = 500
  width = 1000
FEATURE [Part::Part2DObjectPython] Wire009  # Draft 2D object (typed FeaturePython)
  Area = 0
  ChamferSize = 0
  Closed = false
  End = (12940,4850,0)
  FilletRadius = 0
  Length = 16744.3
  MakeFace = false
  Points = (3) [(11129.4,21400.3,0),(12940,13050,0),(12940,4850,0)]
  Start = (11129.4,21400.3,0)
  Subdivisions = 0
FEATURE [Part::FeaturePython] Strip006  label="CSB2"  # Arch/BIM 0 (typed FeaturePython)
  Base = -> Wire009
  HorizontalArea = 0
  IfcData = attributes={"GlobalId": {"name": "GlobalId", "type": "IfcGloballyUniqueId", "is_enum": false, "enum_values": []}, "Description": {"... (+538 chars omitted),+1 more (map truncated)
  IfcType = 0
  MoveBase = false
  MoveWithHost = false
  PerimeterLength = 0
  PredefinedType = 0
  VerticalArea = 0
  align = 0
  design_type = 0
  layer = 1
  left_width = 500
  right_width = 500
  width = 1000
FEATURE [Part::Part2DObjectPython] Line055  # Draft 2D object (typed FeaturePython)
  Area = 0
  ChamferSize = 0
  Closed = false
  End = (17740,20841.8,0)
  FilletRadius = 0
  Length = 15991.8
  MakeFace = false
  Points = (2) [(17740,4850,0),(17740,20841.8,0)]
  Start = (17740,4850,0)
  Subdivisions = 0
FEATURE [Part::FeaturePython] Strip007  label="CSB3"  # Arch/BIM 0 (typed FeaturePython)
  Base = -> Line055
  HorizontalArea = 0
  IfcData = attributes={"GlobalId": {"name": "GlobalId", "type": "IfcGloballyUniqueId", "is_enum": false, "enum_values": []}, "Description": {"... (+538 chars omitted),+1 more (map truncated)
  IfcType = 0
  MoveBase = false
  MoveWithHost = false
  PerimeterLength = 0
  PredefinedType = 0
  VerticalArea = 0
  align = 0
  design_type = 0
  layer = 1
  left_width = 500
  right_width = 500
  width = 1000
FEATURE [Part::Part2DObjectPython] Line056  # Draft 2D object (typed FeaturePython)
  Area = 0
  ChamferSize = 0
  Closed = false
  End = (23870.2,15250,0)
  FilletRadius = 0
  Length = 6630.2
  MakeFace = false
  Points = (2) [(17240,15250,0),(23870.2,15250,0)]
  Start = (17240,15250,0)
  Subdivisions = 0
FEATURE [Part::FeaturePython] Strip008  label="CSA6"  # Arch/BIM 0 (typed FeaturePython)
  Base = -> Line056
  HorizontalArea = 0
  IfcData = attributes={"GlobalId": {"name": "GlobalId", "type": "IfcGloballyUniqueId", "is_enum": false, "enum_values": []}, "Description": {"... (+538 chars omitted),+1 more (map truncated)
  IfcType = 0
  MoveBase = false
  MoveWithHost = false
  PerimeterLength = 0
  PredefinedType = 0
  VerticalArea = 0
  align = 0
  design_type = 0
  layer = 0
  left_width = 500
  right_width = 500
  width = 1000
FEATURE [App::DocumentObjectGroup] A_strips
  Group = -> [Strip001,Strip002,Strip003,Strip004,Strip005,Strip008]
FEATURE [Part::Part2DObjectPython] Line057  # Draft 2D object (typed FeaturePython)
  Area = 0
  ChamferSize = 0
  Closed = false
  End = (23514.2,20339.1,0)
  FilletRadius = 0
  Length = 15495
  MakeFace = false
  Points = (2) [(23086.1,4850,0),(23514.2,20339.1,0)]
  Start = (23086.1,4850,0)
  Subdivisions = 0
FEATURE [Part::FeaturePython] Strip009  label="CSB4"  # Arch/BIM 0 (typed FeaturePython)
  Base = -> Line057
  HorizontalArea = 0
  IfcData = attributes={"GlobalId": {"name": "GlobalId", "type": "IfcGloballyUniqueId", "is_enum": false, "enum_values": []}, "Description": {"... (+538 chars omitted),+1 more (map truncated)
  IfcType = 0
  MoveBase = false
  MoveWithHost = false
  PerimeterLength = 0
  PredefinedType = 0
  VerticalArea = 0
  align = 0
  design_type = 0
  layer = 1
  left_width = 500
  right_width = 500
  width = 1000
FEATURE [App::DocumentObjectGroup] B_strips
  Group = -> [Strip,Strip006,Strip007,Strip009]
FEATURE [App::FeaturePython] Text  # WARN: FeaturePython — macro-defined, semantics opaque (R4)
  Placement = pos=(17740,20897.8,3350) rot=(0,0,1;0rad)
  Text = Edge 3 | 1.74
FEATURE [Part::FeaturePython] Punch  # WARN: FeaturePython — macro-defined, semantics opaque (R4)
  Area = 2.3307e+06
  Av = 400
  Fys = 340000
  I22 = 4.39979e+11
  I23 = 2.26785e+11
  I33 = 7.86181e+11
  Location = 6
  Ratio = 1.74
  Use_Reinforcement = true
  Vc = 2.91338e+09
  Vs = 3.83012e+09
  Vu = 5.05762e+09
  alpha_s = 30
  angle = 0
  b0 = 3007.36
  bx = 550
  by = 550
  center_of_column = (17740,20340,0)
  center_of_load = (17740,20340,0)
  center_of_punch = (17740,20119.2,-387.5)
  column = -> Structure
  combos_ratio = Combo1=1.28,Combo10=0.99,Combo11=0.99,Combo12=1.63,Combo13=1.58,Combo14=1.42,Combo15=1.38,Combo16=1.60,Combo17=1.54,Combo18=1.74,Combo19=1.67,+30 more (map truncated)
  d = 775
  fc = 25000
  foundation = -> Foundation
  gamma_vx = 0.4
  gamma_vy = 0.4
  id = C1_Story1
  one_way_shear_capacity = 1.45669e+09
  s = 27.5187
  text = -> Text
  user_location = false
  vc = 1250
  x = 2105.24
FEATURE [App::FeaturePython] Text001  # WARN: FeaturePython — macro-defined, semantics opaque (R4)
  Placement = pos=(23981.4,19787,3350) rot=(0,0,1;0rad)
  Text = Corner 3 | 1.95
FEATURE [Part::FeaturePython] Punch001  # WARN: FeaturePython — macro-defined, semantics opaque (R4)
  Area = 1.55324e+06
  Av = 400
  Fys = 340000
  I22 = 3.0566e+11
  I23 = 0
  I33 = 2.64378e+11
  Location = 2
  Ratio = 1.95
  Use_Reinforcement = true
  Vc = 1.94155e+09
  Vs = 3.11166e+09
  Vu = 3.78991e+09
  alpha_s = 20
  angle = 0
  b0 = 2004.18
  bx = 550
  by = 550
  center_of_column = (23500,19838.5,0)
  center_of_load = (23500,19838.5,0)
  center_of_punch = (23158.8,19536.7,-387.5)
  column = -> Structure001
  combos_ratio = Combo1=1.33,Combo10=1.43,Combo11=1.49,Combo12=1.15,Combo13=1.09,Combo14=0.83,Combo15=0.78,Combo16=1.95,Combo17=1.88,Combo18=1.76,Combo19=1.68,+30 more (map truncated)
  d = 775
  fc = 25000
  foundation = -> Foundation
  gamma_vx = 0.4
  gamma_vy = 0.4
  id = C2_Story1
  one_way_shear_capacity = 9.70777e+08
  s = 33.8726
  text = -> Text001
  user_location = false
  vc = 1250
  x = 3348.35
FEATURE [App::FeaturePython] Text002  # WARN: FeaturePython — macro-defined, semantics opaque (R4)
  Placement = pos=(23889.7,15250,3350) rot=(0,0,1;0rad)
  Text = Edge 2 | 0.74
FEATURE [Part::FeaturePython] Punch002  # WARN: FeaturePython — macro-defined, semantics opaque (R4)
  Area = 2.32559e+06
  Av = 400
  Fys = 340000
  I22 = 8.36268e+11
  I23 = 2.44443e+11
  I33 = 4.52121e+11
  Location = 5
  Ratio = 0.74
  Use_Reinforcement = false
  Vc = 2.90698e+09
  Vs = 0
  Vu = 2.1628e+09
  alpha_s = 30
  angle = 0
  b0 = 3000.76
  bx = 600
  by = 600
  center_of_column = (23370,15250,0)
  center_of_load = (23370,15250,0)
  center_of_punch = (23141.3,15250,-387.5)
  column = -> Structure002
  combos_ratio = Combo1=0.64,Combo10=0.74,Combo11=0.71,Combo12=0.57,Combo13=0.56,Combo14=0.54,Combo15=0.53,Combo16=0.66,Combo17=0.64,Combo18=0.63,Combo19=0.62,+30 more (map truncated)
  d = 775
  fc = 25000
  foundation = -> Foundation
  gamma_vx = 0.4
  gamma_vy = 0.4
  id = C17_Story1
  one_way_shear_capacity = 1.45349e+09
  s = 0
  text = -> Text002
  user_location = false
  vc = 1250
  x = 0
FEATURE [App::FeaturePython] Text003  # WARN: FeaturePython — macro-defined, semantics opaque (R4)
  Placement = pos=(23768.5,10750,3350) rot=(0,0,1;0rad)
  Text = Edge 2 | 0.78
FEATURE [Part::FeaturePython] Punch003  # WARN: FeaturePython — macro-defined, semantics opaque (R4)
  Area = 2.32557e+06
  Av = 400
  Fys = 340000
  I22 = 8.36262e+11
  I23 = 2.44103e+11
  I33 = 4.51427e+11
  Location = 5
  Ratio = 0.78
  Use_Reinforcement = false
  Vc = 2.90697e+09
  Vs = 0
  Vu = 2.25581e+09
  alpha_s = 30
  angle = 0
  b0 = 3000.74
  bx = 600
  by = 600
  center_of_column = (23250,10750,0)
  center_of_load = (23250,10750,0)
  center_of_punch = (23020.6,10750,-387.5)
  column = -> Structure003
  combos_ratio = Combo1=0.65,Combo10=0.78,Combo11=0.76,Combo12=0.47,Combo13=0.46,Combo14=0.49,Combo15=0.49,Combo16=0.59,Combo17=0.58,Combo18=0.52,Combo19=0.51,+30 more (map truncated)
  d = 775
  fc = 25000
  foundation = -> Foundation
  gamma_vx = 0.4
  gamma_vy = 0.4
  id = C18_Story1
  one_way_shear_capacity = 1.45348e+09
  s = 0
  text = -> Text003
  user_location = false
  vc = 1250
  x = 0
FEATURE [App::FeaturePython] Text004  # WARN: FeaturePython — macro-defined, semantics opaque (R4)
  Placement = pos=(17740,4850,3350) rot=(0,0,1;0rad)
  Text = Edge 1 | 1.10
FEATURE [Part::FeaturePython] Punch004  # WARN: FeaturePython — macro-defined, semantics opaque (R4)
  Area = 2.325e+06
  Av = 400
  Fys = 340000
  I22 = 4.50953e+11
  I23 = 2.44206e+11
  I33 = 8.35991e+11
  Location = 4
  Ratio = 1.1
  Use_Reinforcement = true
  Vc = 2.90625e+09
  Vs = 1.34075e+09
  Vu = 3.18525e+09
  alpha_s = 30
  angle = 0
  b0 = 3000
  bx = 600
  by = 600
  center_of_column = (17740,5350,0)
  center_of_load = (17740,5350,0)
  center_of_punch = (17740,5579.17,-387.5)
  column = -> Structure004
  combos_ratio = Combo1=0.70,Combo10=0.99,Combo11=1.00,Combo12=0.52,Combo13=0.55,Combo14=0.62,Combo15=0.65,Combo16=0.42,Combo17=0.42,Combo18=0.44,Combo19=0.44,+30 more (map truncated)
  d = 775
  fc = 25000
  foundation = -> Foundation
  gamma_vx = 0.4
  gamma_vy = 0.4
  id = C5_Story1
  one_way_shear_capacity = 1.45312e+09
  s = 78.6127
  text = -> Text004
  user_location = false
  vc = 1250
  x = 1182.4
FEATURE [App::FeaturePython] Text005  # WARN: FeaturePython — macro-defined, semantics opaque (R4)
  Placement = pos=(12940,4850,3350) rot=(0,0,1;0rad)
  Text = Edge 1 | 1.40
FEATURE [Part::FeaturePython] Punch005  # WARN: FeaturePython — macro-defined, semantics opaque (R4)
  Area = 2.325e+06
  Av = 400
  Fys = 340000
  I22 = 4.50953e+11
  I23 = 2.44206e+11
  I33 = 8.35991e+11
  Location = 4
  Ratio = 1.4
  Use_Reinforcement = true
  Vc = 2.90625e+09
  Vs = 2.51875e+09
  Vu = 4.06875e+09
  alpha_s = 30
  angle = 0
  b0 = 3000
  bx = 600
  by = 600
  center_of_column = (12940,5350,0)
  center_of_load = (12940,5350,0)
  center_of_punch = (12940,5579.17,-387.5)
  column = -> Structure005
  combos_ratio = Combo1=1.09,Combo10=1.08,Combo11=1.07,Combo12=1.04,Combo13=1.09,Combo14=1.22,Combo15=1.23,Combo16=0.71,Combo17=0.72,Combo18=0.76,Combo19=0.79,+30 more (map truncated)
  d = 775
  fc = 25000
  foundation = -> Foundation
  gamma_vx = 0.4
  gamma_vy = 0.4
  id = C6_Story1
  one_way_shear_capacity = 1.45312e+09
  s = 41.8462
  text = -> Text005
  user_location = false
  vc = 1250
  x = 1617.85
FEATURE [App::FeaturePython] Text006  # WARN: FeaturePython — macro-defined, semantics opaque (R4)
  Placement = pos=(23618.6,5431.25,3350) rot=(0,0,1;0rad)
  Text = Corner 2 | 1.30
FEATURE [Part::FeaturePython] Punch006  # WARN: FeaturePython — macro-defined, semantics opaque (R4)
  Area = 1.5503e+06
  Av = 400
  Fys = 340000
  I22 = 2.73483e+11
  I23 = 0
  I33 = 2.83154e+11
  Location = 1
  Ratio = 1.3
  Use_Reinforcement = true
  Vc = 1.93787e+09
  Vs = 1.43144e+09
  Vu = 2.52699e+09
  alpha_s = 20
  angle = 0
  b0 = 2000.39
  bx = 550
  by = 550
  center_of_column = (23100,5350,0)
  center_of_load = (23100,5350,0)
  center_of_punch = (22778,5681.31,-387.5)
  column = -> Structure006
  combos_ratio = Combo1=0.80,Combo10=1.22,Combo11=1.20,Combo12=0.16,Combo13=0.18,Combo14=0.46,Combo15=0.48,Combo16=0.34,Combo17=0.34,Combo18=0.18,Combo19=0.13,+30 more (map truncated)
  d = 775
  fc = 25000
  foundation = -> Foundation
  gamma_vx = 0.4
  gamma_vy = 0.4
  id = C19_Story1
  one_way_shear_capacity = 9.68937e+08
  s = 73.632
  text = -> Text006
  user_location = false
  vc = 1250
  x = 2103.44
FEATURE [App::FeaturePython] Text007  # WARN: FeaturePython — macro-defined, semantics opaque (R4)
  Placement = pos=(11240,21445.8,3350) rot=(0,0,1;0rad)
  Text = Edge 3 | 1.74
FEATURE [Part::FeaturePython] Punch007  # WARN: FeaturePython — macro-defined, semantics opaque (R4)
  Area = 2.34819e+06
  Av = 400
  Fys = 340000
  I22 = 4.60028e+11
  I23 = 2.87438e+11
  I33 = 8.55594e+11
  Location = 6
  Ratio = 1.74
  Use_Reinforcement = true
  Vc = 2.93523e+09
  Vs = 3.89016e+09
  Vu = 5.11905e+09
  alpha_s = 30
  angle = 0
  b0 = 3029.92
  bx = 600
  by = 600
  center_of_column = (11240,20890,0)
  center_of_load = (11240,20890,0)
  center_of_punch = (11290.5,20656.5,-387.5)
  column = -> Structure007
  combos_ratio = Combo1=1.39,Combo10=1.42,Combo11=1.38,Combo12=1.50,Combo13=1.50,Combo14=1.30,Combo15=1.30,Combo16=1.74,Combo17=1.74,Combo18=1.74,Combo19=1.74,+30 more (map truncated)
  d = 775
  fc = 25000
  foundation = -> Foundation
  gamma_vx = 0.4
  gamma_vy = 0.4
  id = C8_Story1
  one_way_shear_capacity = 1.46762e+09
  s = 27.094
  text = -> Text007
  user_location = false
  vc = 1250
  x = 2135.51
FEATURE [App::FeaturePython] Text008  # WARN: FeaturePython — macro-defined, semantics opaque (R4)
  Placement = pos=(6930,21675.3,3350) rot=(0,0,1;0rad)
  Text = Edge 3 | 2.43
FEATURE [Part::FeaturePython] Punch008  # WARN: FeaturePython — macro-defined, semantics opaque (R4)
  Area = 1.87204e+06
  Av = 400
  Fys = 340000
  I22 = 2.936e+11
  I23 = 2.31599e+11
  I33 = 8.04502e+11
  Location = 6
  Ratio = 2.43
  Use_Reinforcement = true
  Vc = 2.34005e+09
  Vs = 5.24794e+09
  Vu = 5.69099e+09
  Warnings = Vs > 2 * Vc
  alpha_s = 30
  angle = 0
  b0 = 2415.53
  bx = 650
  by = 650
  center_of_column = (6930,21230,0)
  center_of_load = (6930,21230,0)
  center_of_punch = (6902.36,20903.9,-387.5)
  column = -> Structure008
  combos_ratio = Combo1=1.67,Combo10=1.32,Combo11=1.27,Combo12=2.24,Combo13=2.26,Combo14=1.86,Combo15=1.86,Combo16=2.18,Combo17=2.20,Combo18=2.42,Combo19=2.43,+30 more (map truncated)
  d = 775
  fc = 25000
  foundation = -> Foundation
  gamma_vx = 0.4
  gamma_vy = 0.4
  id = C9_Story1
  one_way_shear_capacity = 1.17002e+09
  s = 20.0841
  text = -> Text008
  user_location = false
  vc = 1250
  x = 2417.4
FEATURE [App::FeaturePython] Text009  # WARN: FeaturePython — macro-defined, semantics opaque (R4)
  Placement = pos=(2400,17580,3350) rot=(0,0,1;0rad)
  Text = Edge 4 | 2.11
FEATURE [Part::FeaturePython] Punch009  # WARN: FeaturePython — macro-defined, semantics opaque (R4)
  Area = 2.56381e+06
  Av = 400
  Fys = 340000
  I22 = 9.48133e+11
  I23 = 2.3381e+11
  I33 = 3.9558e+11
  Location = 7
  Ratio = 2.11
  Use_Reinforcement = true
  Vc = 3.20477e+09
  Vs = 5.81986e+09
  Vu = 6.76847e+09
  alpha_s = 30
  angle = 0
  b0 = 3308.15
  bx = 650
  by = 650
  center_of_column = (2900,17580,0)
  center_of_load = (2900,17580,0)
  center_of_punch = (3322.32,17463.3,-387.5)
  column = -> Structure009
  combos_ratio = Combo1=1.83,Combo10=1.55,Combo11=1.57,Combo12=2.10,Combo13=2.08,Combo14=2.11,Combo15=2.10,Combo16=1.74,Combo17=1.72,Combo18=1.90,Combo19=1.88,+30 more (map truncated)
  d = 775
  fc = 25000
  foundation = -> Foundation
  gamma_vx = 0.4
  gamma_vy = 0.4
  id = C10_Story1
  one_way_shear_capacity = 1.60238e+09
  s = 18.1104
  text = -> Text009
  user_location = false
  vc = 1250
  x = 2948.45
FEATURE [App::FeaturePython] Text010  # WARN: FeaturePython — macro-defined, semantics opaque (R4)
  Placement = pos=(2400,5456.25,3350) rot=(0,0,1;0rad)
  Text = Corner 1 | 2.79
FEATURE [Part::FeaturePython] Punch010  # WARN: FeaturePython — macro-defined, semantics opaque (R4)
  Area = 1.55e+06
  Av = 400
  Fys = 340000
  I22 = 3.0009e+11
  I23 = 0
  I33 = 3.0009e+11
  Location = 0
  Ratio = 2.79
  Use_Reinforcement = true
  Vc = 1.9375e+09
  Vs = 5.27517e+09
  Vu = 5.4095e+09
  Warnings = Vs > 2 * Vc
  alpha_s = 20
  angle = 0
  b0 = 2000
  bx = 650
  by = 650
  center_of_column = (2900,5350,0)
  center_of_load = (2900,5350,0)
  center_of_punch = (3256.25,5706.25,-387.5)
  column = -> Structure010
  combos_ratio = Combo1=1.68,Combo10=1.93,Combo11=2.08,Combo12=1.29,Combo13=1.14,Combo14=1.93,Combo15=1.78,Combo16=0.66,Combo17=0.54,Combo18=0.62,Combo19=0.67,+30 more (map truncated)
  d = 775
  fc = 25000
  foundation = -> Foundation
  gamma_vx = 0.4
  gamma_vy = 0.4
  id = C16_Story1
  one_way_shear_capacity = 9.6875e+08
  s = 19.9804
  text = -> Text010
  user_location = false
  vc = 1250
  x = 4944.83
FEATURE [App::FeaturePython] Text011  # WARN: FeaturePython — macro-defined, semantics opaque (R4)
  Placement = pos=(17740,11437.5,3350) rot=(0,0,1;0rad)
  Text = Interior | 0.77
FEATURE [Part::FeaturePython] Punch011  # WARN: FeaturePython — macro-defined, semantics opaque (R4)
  Area = 3.1e+06
  Av = 400
  Fys = 340000
  I22 = 9.39365e+11
  I23 = 0
  I33 = 9.39365e+11
  Location = 8
  Ratio = 0.77
  Use_Reinforcement = false
  Vc = 3.875e+09
  Vs = 0
  Vu = 2.976e+09
  alpha_s = 40
  angle = 0
  b0 = 4000
  bx = 600
  by = 600
  center_of_column = (17740,10750,0)
  center_of_load = (17740,10750,0)
  center_of_punch = (17740,10750,-387.5)
  column = -> Structure011
  combos_ratio = Combo1=0.62,Combo10=0.74,Combo11=0.74,Combo12=0.64,Combo13=0.64,Combo14=0.67,Combo15=0.68,Combo16=0.63,Combo17=0.62,Combo18=0.62,Combo19=0.62,+30 more (map truncated)
  d = 775
  fc = 25000
  foundation = -> Foundation
  gamma_vx = 0.4
  gamma_vy = 0.4
  id = C12_Story1
  one_way_shear_capacity = 1.9375e+09
  s = 0
  text = -> Text011
  user_location = false
  vc = 1250
  x = 0
FEATURE [App::FeaturePython] Text012  # WARN: FeaturePython — macro-defined, semantics opaque (R4)
  Placement = pos=(17240,15250,3350) rot=(0,0,1;0rad)
  Text = Edge 4 | 1.18
FEATURE [Part::FeaturePython] Punch012  # WARN: FeaturePython — macro-defined, semantics opaque (R4)
  Area = 2.325e+06
  Av = 400
  Fys = 340000
  I22 = 7.83678e+11
  I23 = 2.26768e+11
  I33 = 4.33516e+11
  Location = 7
  Ratio = 1.18
  Use_Reinforcement = true
  Vc = 2.90625e+09
  Vs = 1.68175e+09
  Vu = 3.441e+09
  alpha_s = 30
  angle = 0
  b0 = 3000
  bx = 550
  by = 550
  center_of_column = (17740,15250,0)
  center_of_load = (17740,15250,0)
  center_of_punch = (17960.8,15250,-387.5)
  column = -> Structure012
  combos_ratio = Combo1=1.10,Combo10=1.06,Combo11=1.06,Combo12=1.02,Combo13=1.02,Combo14=0.99,Combo15=0.99,Combo16=1.11,Combo17=1.11,Combo18=1.10,Combo19=1.10,+30 more (map truncated)
  d = 775
  fc = 25000
  foundation = -> Foundation
  gamma_vx = 0.4
  gamma_vy = 0.4
  id = C13_Story1
  one_way_shear_capacity = 1.45312e+09
  s = 62.6728
  text = -> Text012
  user_location = false
  vc = 1250
  x = 1308.46
FEATURE [App::FeaturePython] Text013  # WARN: FeaturePython — macro-defined, semantics opaque (R4)
  Placement = pos=(12940,11387.5,3350) rot=(0,0,1;1.5708rad)
  Text = Interior | 1.02
FEATURE [Part::FeaturePython] Punch013  # WARN: FeaturePython — macro-defined, semantics opaque (R4)
  Area = 3.1e+06
  Av = 400
  Fys = 340000
  I22 = 8.36677e+11
  I23 = 0.00179739
  I33 = 8.36677e+11
  Location = 8
  Ratio = 1.02
  Use_Reinforcement = true
  Vc = 3.875e+09
  Vs = 1.37433e+09
  Vu = 3.937e+09
  alpha_s = 40
  angle = 90
  b0 = 4000
  bx = 500
  by = 500
  center_of_column = (12940,10750,0)
  center_of_load = (12940,10750,0)
  center_of_punch = (12940,10750,-387.5)
  column = -> Structure013
  combos_ratio = Combo1=0.69,Combo10=0.72,Combo11=0.71,Combo12=0.74,Combo13=0.75,Combo14=0.88,Combo15=0.89,Combo16=0.47,Combo17=0.48,Combo18=0.54,Combo19=0.55,+30 more (map truncated)
  d = 775
  fc = 25000
  foundation = -> Foundation
  gamma_vx = 0.4
  gamma_vy = 0.4
  id = C14_Story1
  one_way_shear_capacity = 1.9375e+09
  s = 76.6917
  text = -> Text013
  user_location = false
  vc = 1250
  x = 582.709
FEATURE [App::FeaturePython] Text014  # WARN: FeaturePython — macro-defined, semantics opaque (R4)
  Placement = pos=(12940,13687.5,3350) rot=(0,0,1;1.5708rad)
  Text = Interior | 1.08
FEATURE [Part::FeaturePython] Punch014  # WARN: FeaturePython — macro-defined, semantics opaque (R4)
  Area = 3.0297e+06
  Av = 400
  Fys = 340000
  I22 = 8.19958e+11
  I23 = 1.47135e+11
  I33 = 8.36951e+11
  Location = 8
  Ratio = 1.08
  Use_Reinforcement = true
  Vc = 3.78712e+09
  Vs = 1.66633e+09
  Vu = 4.09009e+09
  alpha_s = 40
  angle = 90
  b0 = 3909.29
  bx = 500
  by = 500
  center_of_column = (12940,13050,0)
  center_of_load = (12940,13050,0)
  center_of_punch = (12985,13067.6,-387.5)
  column = -> Structure014
  combos_ratio = Combo1=0.90,Combo10=0.83,Combo11=0.83,Combo12=0.97,Combo13=0.97,Combo14=0.87,Combo15=0.87,Combo16=1.08,Combo17=1.08,Combo18=1.08,Combo19=1.08,+30 more (map truncated)
  d = 775
  fc = 25000
  foundation = -> Foundation
  gamma_vx = 0.4
  gamma_vy = 0.4
  id = C15_Story1
  one_way_shear_capacity = 1.89356e+09
  s = 63.2526
  text = -> Text014
  user_location = false
  vc = 1250
  x = 620.436
FEATURE [App::FeaturePython] Text015  # WARN: FeaturePython — macro-defined, semantics opaque (R4)
  Placement = pos=(2400,10750,3350) rot=(0,0,1;0rad)
  Text = Edge 4 | 1.55
FEATURE [Part::FeaturePython] Punch015  # WARN: FeaturePython — macro-defined, semantics opaque (R4)
  Area = 2.325e+06
  Av = 400
  Fys = 340000
  I22 = 8.90241e+11
  I23 = 2.62289e+11
  I33 = 4.69036e+11
  Location = 7
  Ratio = 1.55
  Use_Reinforcement = true
  Vc = 2.90625e+09
  Vs = 3.10775e+09
  Vu = 4.5105e+09
  alpha_s = 30
  angle = 0
  b0 = 3000
  bx = 650
  by = 650
  center_of_column = (2900,10750,0)
  center_of_load = (2900,10750,0)
  center_of_punch = (3137.5,10750,-387.5)
  column = -> Structure015
  combos_ratio = Combo1=1.42,Combo10=1.50,Combo11=1.51,Combo12=1.30,Combo13=1.30,Combo14=1.28,Combo15=1.26,Combo16=1.48,Combo17=1.48,Combo18=1.41,Combo19=1.41,+30 more (map truncated)
  d = 775
  fc = 25000
  foundation = -> Foundation
  gamma_vx = 0.4
  gamma_vy = 0.4
  id = C11_Story1
  one_way_shear_capacity = 1.45312e+09
  s = 33.9152
  text = -> Text015
  user_location = false
  vc = 1250
  x = 1835.58
FEATURE [App::DocumentObjectGroup] Punches
  Group = -> [Punch,Punch001,Punch002,Punch003,Punch004,Punch005,Punch006,Punch007,Punch008,Punch009,Punch010,Punch011,Punch012,Punch013,Punch014,Punch015]
note: 2 file-system paths scrubbed to <path> (originals preserved in the JSON sidecar)
